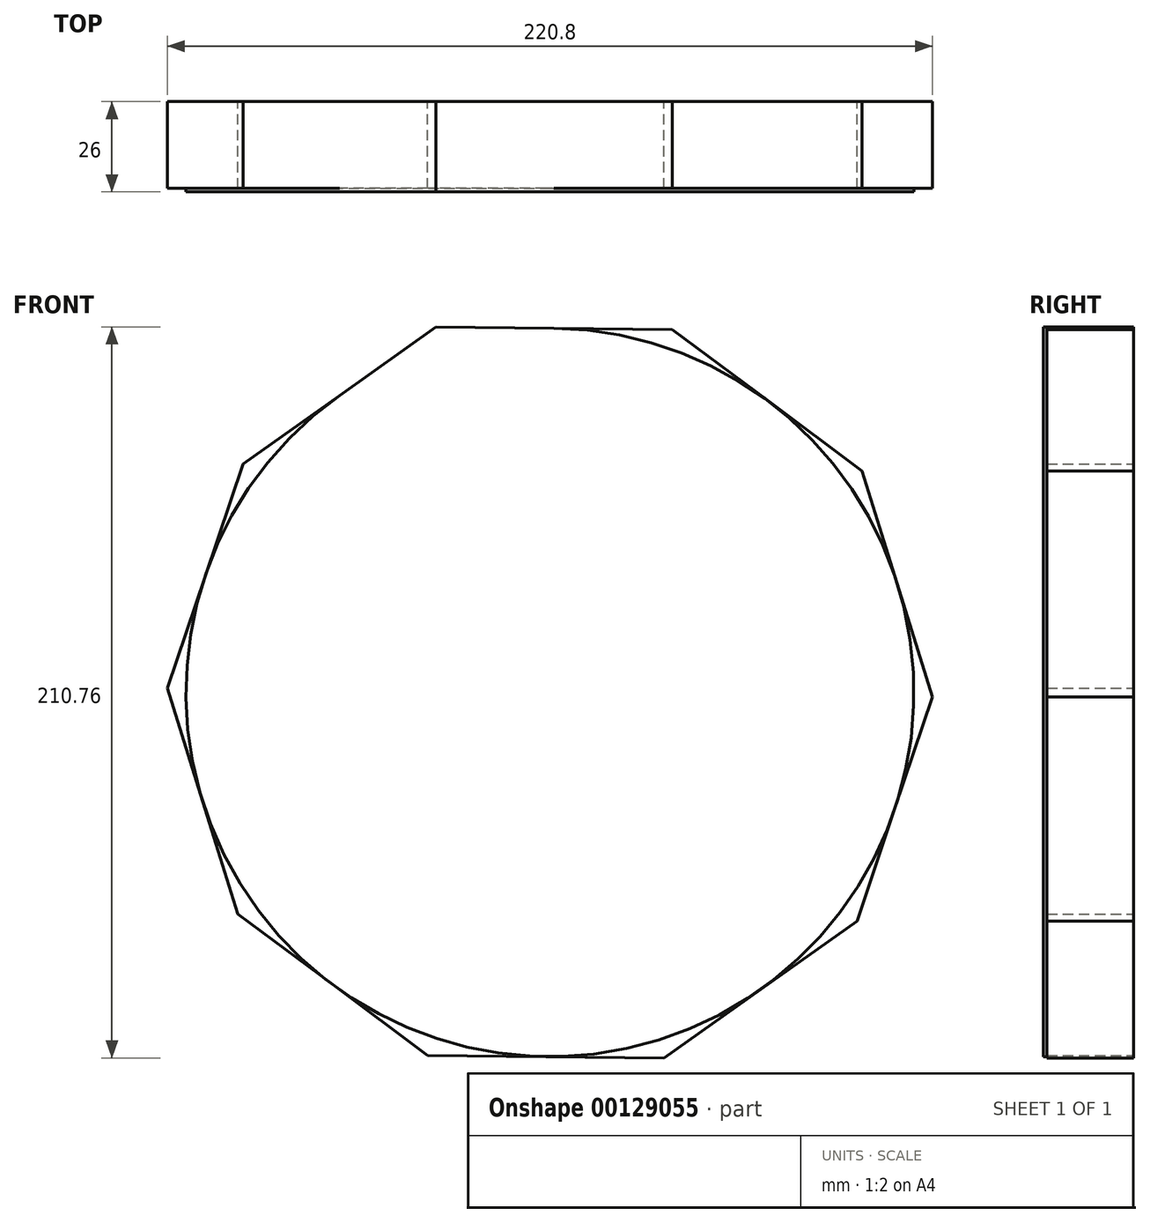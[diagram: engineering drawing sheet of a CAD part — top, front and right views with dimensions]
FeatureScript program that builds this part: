
annotation { "Feature Type Name" : "Feature", "Feature Type Description" : "" }
export const myFeature = defineFeature(function(context is Context, id is Id, definition is map)
    precondition{}
    {
        {
            var Q0;
            Q0=qCreatedBy(makeId("Front.planeOp"),FACE);
            var sketch = newSketch(context, id + "F0", { "sketchPlane" : qUnion([Q0])});
            skCircle(sketch, "E0", {"center": v(0, 0) * mm, "radius": 105 * mm});
            skCircle(sketch, "E1.cCircle", {"center": v(0, 0) * mm, "radius": 105 * mm, "construction": true});
            skLineSegment(sketch, "E1.0", {"start": v(90.04, 63.89) * mm, "end": v(110.4, -1.24) * mm});
            skLineSegment(sketch, "E1.1", {"start": v(110.4, -1.24) * mm, "end": v(88.58, -65.9) * mm});
            skLineSegment(sketch, "E1.2", {"start": v(88.58, -65.9) * mm, "end": v(32.94, -105.38) * mm});
            skLineSegment(sketch, "E1.3", {"start": v(32.94, -105.38) * mm, "end": v(-35.3, -104.61) * mm});
            skLineSegment(sketch, "E1.4", {"start": v(-35.3, -104.61) * mm, "end": v(-90.04, -63.89) * mm});
            skLineSegment(sketch, "E1.5", {"start": v(-90.04, -63.89) * mm, "end": v(-110.4, 1.24) * mm});
            skLineSegment(sketch, "E1.6", {"start": v(-110.4, 1.24) * mm, "end": v(-88.58, 65.9) * mm});
            skLineSegment(sketch, "E1.7", {"start": v(-88.58, 65.9) * mm, "end": v(-32.94, 105.38) * mm});
            skLineSegment(sketch, "E1.8", {"start": v(-32.94, 105.38) * mm, "end": v(35.3, 104.61) * mm});
            skLineSegment(sketch, "E1.9", {"start": v(35.3, 104.61) * mm, "end": v(90.04, 63.89) * mm});
            skPoint(sketch, "E1.0.midPoint", {"position": v(100.22, 31.32) * mm});
            skSolve(sketch);
        }
        {
            var Q0;
            {var subQ0=sQuery(id+"F0.wireOp",EDGE,"E0");var subQ6=makeQuery(id+"F0.imprint","INTERSECT",VERTEX,{"derivedFrom":[subQ0,sQuery(id+"F0.wireOp",EDGE,"E1.9")]});Q0=makeQuery(id+"F0.imprint","IMPRINT",FACE,{"disambiguationData":[TD([[makeQuery(id+"F0.imprint","IMPRINT",EDGE,{"disambiguationData":[TD([[subQ6,1.0]])],"derivedFrom":subQ0}),1.0]])]});}
            var Q1;
            {var subQ0=sQuery(id+"F0.wireOp",EDGE,"E1.8");var subQ1=sQuery(id+"F0.wireOp",EDGE,"E0");var subQ2=makeQuery(id+"F0.imprint","INTERSECT",VERTEX,{"derivedFrom":[subQ1,subQ0]});Q1=makeQuery(id+"F0.imprint","IMPRINT",FACE,{"disambiguationData":[TD([[makeQuery(id+"F0.imprint","IMPRINT",EDGE,{"disambiguationData":[TD([[subQ2,-1.0]])],"derivedFrom":subQ1}),-1.0]])]});}
            extrude(context, id + "F1", {"entities" : qUnion([Q0, Q1]), "depth" : 1 * mm});
        }
        {
            var Q0;
            Q0 = qSketchRegion(id + "F0", true);
            var Q1;
            Q1=makeQuery(id+"F1.opExtrude","CAP_FACE",FACE,{"disambiguationData":[OSD([sQuery(id+"F0.wireOp",EDGE,"E0"),sQuery(id+"F0.wireOp",EDGE,"E1.7"),sQuery(id+"F0.wireOp",EDGE,"E1.8")])],"isStart":false});
            extrude(context, id + "F2", {"entities" : qUnion([Q0, Q1]), "operationType" : NewBodyOperationType.ADD, "depth" : 25 * mm});
        }
    });
